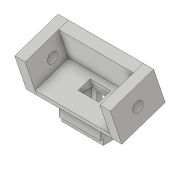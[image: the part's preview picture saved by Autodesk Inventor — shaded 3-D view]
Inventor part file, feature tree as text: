
AUTODESK INVENTOR PART (.ipt)
format: ipt  version: 2018.3 (Build 223284000, 284)  size: 291,840 bytes
history: native  units: in
note: dims shown in document units (in); Inventor stores cm internally (conversion verified against a paired STEP export)
features: extrude x15, sketch x15, plane x1
ambient origin geometry x8: Origin, YZ Plane, XZ Plane, XY Plane, X Axis, Y Axis, Z Axis, Center Point
bodies: Body1 (feature_tree)
feature tree (31):
  extrude  "Extrusion6"  Depth=0.25in TaperAngle=0.0deg
  extrude  "Extrusion8"  Depth=0.5in
  extrude  "Extrusion10"  Depth=0.65in
  extrude  "Extrusion11"  Depth=1.8in TaperAngle=0.0deg
  extrude  "Extrusion12"  Depth=0.25in
  extrude  "Extrusion13"  TaperAngle=0.0deg  [1 undecoded]
  extrude  "Extrusion14"  Depth=1.1in
  extrude  "Extrusion15"  Depth=0.25in TaperAngle=0.0deg
  extrude  "Extrusion16"  Depth=0.125in TaperAngle=0.0deg
  extrude  "Extrusion17"  Depth=1.8in TaperAngle=0.0deg
  plane  "Work Plane1"
  extrude  "Extrusion18"  Depth=0.75in
  extrude  "Extrusion19"  Depth=0.25in TaperAngle=0.0deg
  extrude  "Extrusion20"  Depth=0.125in
  extrude  "Extrusion21"  Depth=0.125in
  extrude  "Extrusion22"  Depth=0.125in
  sketch  "Sketch8"  dims[d40=1.8in d41=0.0in d50=0.25in d51=0.0in]
  sketch  "Sketch11"  dims[d55=0.3in d56=0.5in]
  sketch  "Sketch13"  dims[d57=0.65in d58=0.65in]
  sketch  "Sketch15"  dims[d59=1.0in d60=0.0in d62=1.8in d63=0.0in]
  sketch  "Sketch17"  dims[d67=0.25in d68=0.1274in]
  sketch  "Sketch19"  dims[d69=0.0in d70=0.0in]
  sketch  "Sketch20"  dims[d73=1.1in d74=0.1274in]
  sketch  "Sketch21"  dims[d76=0.0in d77=0.25in d78=0.0in]
  sketch  "Sketch22"  dims[d79=0.125in d80=0.0in d81=0.125in d82=0.0in]
  sketch  "Sketch23"  dims[d83=1.8in d84=0.0in d85=1.8in d86=0.0in]
  sketch  "Sketch25"  dims[d87=0.75in d88=0.75in]
  sketch  "Sketch26"  dims[d89=0.25in d90=3.0in d91=0.0in]
  sketch  "Sketch27"  dims[d100=-0.1274in d102=0.125in]
  sketch  "Sketch28"  dims[d103=0.125in d104=0.125in]
  sketch  "Sketch29"  dims[d105=0.125in d106=0.125in d107=0.125in d108=0.125in d109=0.125in d110=0.15in d111=0.0in d112=1.0in d113=0.0in d114=1.0in d115=0.0in d116=0.25in d117=0.25in d118=0.325in d119=0.0in d121=0.125in d122=0.0in d124=0.0625in]
note: 1 required parameter value undecoded (feature->parameter linkage not recoverable at this tier; creation-order binding heuristic only, values carry confidence <= 0.55)
